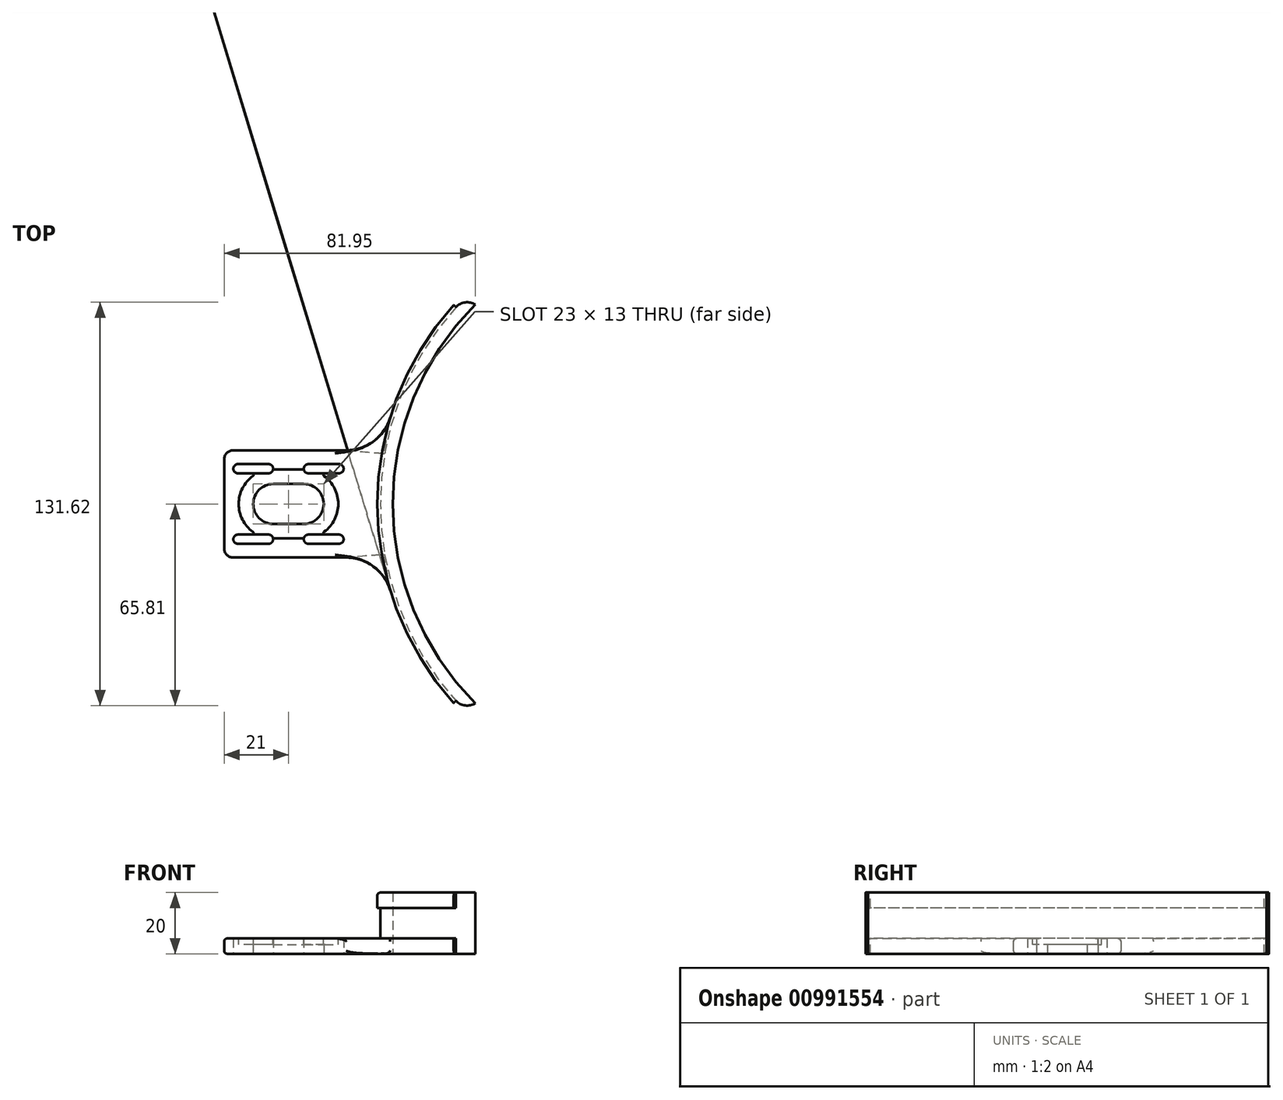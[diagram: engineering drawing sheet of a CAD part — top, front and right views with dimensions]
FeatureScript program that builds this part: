
annotation { "Feature Type Name" : "Feature", "Feature Type Description" : "" }
export const myFeature = defineFeature(function(context is Context, id is Id, definition is map)
    precondition{}
    {
        {
            var Q0;
            Q0=qCreatedBy(makeId("Top.planeOp"),FACE);
            var sketch = newSketch(context, id + "F0", { "sketchPlane" : qUnion([Q0])});
            skPoint(sketch, "E0", {"position": v(92, 0) * mm});
            skLineSegment(sketch, "E1", {"start": v(92, 0) * mm, "end": v(-64.87, 0) * mm, "construction": true});
            skLineSegment(sketch, "E2", {"start": v(92, 0) * mm, "end": v(-16.43, 108.43) * mm, "construction": true});
            skLineSegment(sketch, "E3", {"start": v(92, 0) * mm, "end": v(-13.59, -105.59) * mm, "construction": true});
            skArc(sketch, "E4", {"start": v(26.95, 65.05) * mm, "mid": v(0, 0) * mm, "end": v(26.95, -65.05) * mm});
            skArc(sketch, "E5", {"start": v(24.12, 67.88) * mm, "mid": v(-4, 0) * mm, "end": v(24.12, -67.88) * mm});
            skLineSegment(sketch, "E6", {"start": v(26.95, 65.05) * mm, "end": v(24.12, 67.88) * mm});
            skLineSegment(sketch, "E7", {"start": v(26.95, -65.05) * mm, "end": v(24.12, -67.88) * mm});
            skSolve(sketch);
        }
        {
            var Q0;
            Q0 = qSketchRegion(id + "F0", true);
            extrude(context, id + "F1", {"entities" : qUnion([Q0]), "depth" : 20 * mm, "offsetDistance" : 25 * mm});
        }
        {
            var Q0;
            Q0=qCreatedBy(makeId("Top.planeOp"),FACE);
            var sketch = newSketch(context, id + "F2", { "sketchPlane" : qUnion([Q0])});
            skLineSegment(sketch, "E8.bottom", {"start": v(0, 17.5) * mm, "end": v(-55, 17.5) * mm});
            skLineSegment(sketch, "E8.top", {"start": v(0, -17.5) * mm, "end": v(-55, -17.5) * mm});
            skLineSegment(sketch, "E8.left", {"start": v(0, 17.5) * mm, "end": v(0, -17.5) * mm});
            skLineSegment(sketch, "E8.right", {"start": v(-55, 17.5) * mm, "end": v(-55, -17.5) * mm});
            skPoint(sketch, "E8.middle", {"position": v(-27.5, 0) * mm});
            skSolve(sketch);
        }
        {
            var Q0;
            Q0 = qSketchRegion(id + "F2", true);
            extrude(context, id + "F3", {"entities" : qUnion([Q0]), "operationType" : NewBodyOperationType.ADD, "depth" : 5 * mm, "offsetDistance" : 25 * mm});
        }
        {
            var Q0;
            Q0=makeQuery(id+"F1.opExtrude","CAP_FACE",FACE,{"disambiguationData":[OSD([sQuery(id+"F0.wireOp",EDGE,"E4"),sQuery(id+"F0.wireOp",EDGE,"E5"),sQuery(id+"F0.wireOp",EDGE,"E6"),sQuery(id+"F0.wireOp",EDGE,"E7")])],"isStart":false});
            var sketch = newSketch(context, id + "F4", { "sketchPlane" : qUnion([Q0])});
            skPoint(sketch, "E9", {"position": v(92, 0) * mm});
            skLineSegment(sketch, "E10", {"start": v(92, 0) * mm, "end": v(-2.81, -85.37) * mm, "construction": true});
            skLineSegment(sketch, "E11", {"start": v(92, 0) * mm, "end": v(-2.76, 85.32) * mm, "construction": true});
            skArc(sketch, "E12", {"start": v(20.66, 64.24) * mm, "mid": v(-4, 0) * mm, "end": v(20.66, -64.24) * mm});
            skArc(sketch, "E13", {"start": v(19.91, 64.9) * mm, "mid": v(-5, 0) * mm, "end": v(19.91, -64.9) * mm});
            skLineSegment(sketch, "E14", {"start": v(19.91, 64.9) * mm, "end": v(20.66, 64.24) * mm});
            skLineSegment(sketch, "E15", {"start": v(19.91, -64.9) * mm, "end": v(20.66, -64.24) * mm});
            skSolve(sketch);
        }
        {
            var Q0;
            Q0 = qSketchRegion(id + "F4", true);
            extrude(context, id + "F5", {"entities" : qUnion([Q0]), "operationType" : NewBodyOperationType.ADD, "oppositeDirection" : true, "depth" : 5 * mm, "offsetDistance" : 25 * mm});
        }
        {
            var Q0;
            Q0=makeQuery(id+"F3.boolean.opBoolean","MERGE",FACE,{"derivedFrom":[makeQuery(id+"F1.opExtrude","CAP_FACE",FACE,{"disambiguationData":[OSD([sQuery(id+"F0.wireOp",EDGE,"E4"),sQuery(id+"F0.wireOp",EDGE,"E5"),sQuery(id+"F0.wireOp",EDGE,"E6"),sQuery(id+"F0.wireOp",EDGE,"E7")])],"isStart":true}),makeQuery(id+"F3.opExtrude","CAP_FACE",FACE,{"disambiguationData":[OSD([sQuery(id+"F2.wireOp",EDGE,"E8.bottom"),sQuery(id+"F2.wireOp",EDGE,"E8.top"),sQuery(id+"F2.wireOp",EDGE,"E8.left"),sQuery(id+"F2.wireOp",EDGE,"E8.right")])],"isStart":true})]});
            var Q1;
            Q1=makeQuery(id+"F3.boolean.opBoolean","MERGE",FACE,{"derivedFrom":[makeQuery(id+"F1.opExtrude","CAP_FACE",FACE,{"disambiguationData":[OSD([sQuery(id+"F0.wireOp",EDGE,"E4"),sQuery(id+"F0.wireOp",EDGE,"E5"),sQuery(id+"F0.wireOp",EDGE,"E6"),sQuery(id+"F0.wireOp",EDGE,"E7")])],"isStart":true}),makeQuery(id+"F3.opExtrude","CAP_FACE",FACE,{"disambiguationData":[OSD([sQuery(id+"F2.wireOp",EDGE,"E8.bottom"),sQuery(id+"F2.wireOp",EDGE,"E8.top"),sQuery(id+"F2.wireOp",EDGE,"E8.left"),sQuery(id+"F2.wireOp",EDGE,"E8.right")])],"isStart":true})]});
            var sketch = newSketch(context, id + "F6", { "sketchPlane" : qUnion([Q0, Q1])});
            skPoint(sketch, "E16", {"position": v(92, 0) * mm});
            skLineSegment(sketch, "E17", {"start": v(92, 0) * mm, "end": v(6.61, -76.88) * mm, "construction": true});
            skLineSegment(sketch, "E18", {"start": v(92, 0) * mm, "end": v(0.37, 82.5) * mm, "construction": true});
            skLineSegment(sketch, "E19", {"start": v(92, 0) * mm, "end": v(0, 0) * mm, "construction": true});
            skArc(sketch, "E20", {"start": v(20.66, 64.24) * mm, "mid": v(-4, 0) * mm, "end": v(20.66, -64.24) * mm});
            skArc(sketch, "E21", {"start": v(19.91, 64.9) * mm, "mid": v(-5, 0) * mm, "end": v(19.91, -64.9) * mm});
            skLineSegment(sketch, "E22", {"start": v(19.91, 64.9) * mm, "end": v(20.66, 64.24) * mm});
            skLineSegment(sketch, "E23", {"start": v(19.91, -64.9) * mm, "end": v(20.66, -64.24) * mm});
            skSolve(sketch);
        }
        {
            var Q0;
            Q0 = qSketchRegion(id + "F6", true);
            extrude(context, id + "F7", {"entities" : qUnion([Q0]), "operationType" : NewBodyOperationType.ADD, "oppositeDirection" : true, "depth" : 5 * mm, "offsetDistance" : 25 * mm});
        }
        {
            var Q0;
            Q0=makeQuery(id+"F7.boolean.opBoolean","MERGE",FACE,{"derivedFrom":[makeQuery(id+"F3.boolean.opBoolean","MERGE",FACE,{"derivedFrom":[makeQuery(id+"F1.opExtrude","CAP_FACE",FACE,{"disambiguationData":[OSD([sQuery(id+"F0.wireOp",EDGE,"E4"),sQuery(id+"F0.wireOp",EDGE,"E5"),sQuery(id+"F0.wireOp",EDGE,"E6"),sQuery(id+"F0.wireOp",EDGE,"E7")])],"isStart":true}),makeQuery(id+"F3.opExtrude","CAP_FACE",FACE,{"disambiguationData":[OSD([sQuery(id+"F2.wireOp",EDGE,"E8.bottom"),sQuery(id+"F2.wireOp",EDGE,"E8.top"),sQuery(id+"F2.wireOp",EDGE,"E8.left"),sQuery(id+"F2.wireOp",EDGE,"E8.right")])],"isStart":true})]}),makeQuery(id+"F7.opExtrude","CAP_FACE",FACE,{"disambiguationData":[OSD([sQuery(id+"F6.wireOp",EDGE,"E20"),sQuery(id+"F6.wireOp",EDGE,"E21"),sQuery(id+"F6.wireOp",EDGE,"E22"),sQuery(id+"F6.wireOp",EDGE,"E23")])],"isStart":true})]});
            var sketch = newSketch(context, id + "F8", { "sketchPlane" : qUnion([Q0])});
            skPoint(sketch, "E24", {"position": v(-34, 0) * mm});
            skLineSegment(sketch, "E25", {"start": v(-39, 0) * mm, "end": v(-29, 0) * mm, "construction": true});
            skArc(sketch, "E26.0.startCap", {"start": v(-39, -6.5) * mm, "mid": v(-45.5, 0) * mm, "end": v(-39, 6.5) * mm});
            skArc(sketch, "E26.0.endCap", {"start": v(-29, 6.5) * mm, "mid": v(-22.5, 0) * mm, "end": v(-29, -6.5) * mm});
            skLineSegment(sketch, "E26.0.left", {"start": v(-39, 6.5) * mm, "end": v(-29, 6.5) * mm});
            skLineSegment(sketch, "E26.0.right", {"start": v(-39, -6.5) * mm, "end": v(-29, -6.5) * mm});
            skLineSegment(sketch, "E27", {"start": v(-34, 14.73) * mm, "end": v(-34, -13.9) * mm, "construction": true});
            skLineSegment(sketch, "E28", {"start": v(-53.74, 0) * mm, "end": v(-13.22, 0) * mm, "construction": true});
            skLineSegment(sketch, "E29", {"start": v(-29, 25.63) * mm, "end": v(-29, -27.09) * mm, "construction": true});
            skLineSegment(sketch, "E30", {"start": v(-39, -27.74) * mm, "end": v(-39, 26.77) * mm, "construction": true});
            skLineSegment(sketch, "E31", {"start": v(-17.5, 11.5) * mm, "end": v(-27.5, 11.5) * mm, "construction": true});
            skLineSegment(sketch, "E32", {"start": v(-17.5, -11.5) * mm, "end": v(-27.5, -11.5) * mm, "construction": true});
            skLineSegment(sketch, "E33", {"start": v(-40.5, -11.5) * mm, "end": v(-50.5, -11.5) * mm, "construction": true});
            skLineSegment(sketch, "E34", {"start": v(-40.5, 11.5) * mm, "end": v(-50.5, 11.5) * mm, "construction": true});
            skArc(sketch, "E35.0.startCap", {"start": v(-17.5, 13) * mm, "mid": v(-16, 11.5) * mm, "end": v(-17.5, 10) * mm});
            skArc(sketch, "E35.0.endCap", {"start": v(-27.5, 10) * mm, "mid": v(-29, 11.5) * mm, "end": v(-27.5, 13) * mm});
            skLineSegment(sketch, "E35.0.left", {"start": v(-17.5, 10) * mm, "end": v(-27.5, 10) * mm});
            skLineSegment(sketch, "E35.0.right", {"start": v(-17.5, 13) * mm, "end": v(-27.5, 13) * mm});
            skArc(sketch, "E36.0.startCap", {"start": v(-40.5, 13) * mm, "mid": v(-39, 11.5) * mm, "end": v(-40.5, 10) * mm});
            skArc(sketch, "E36.0.endCap", {"start": v(-50.5, 10) * mm, "mid": v(-52, 11.5) * mm, "end": v(-50.5, 13) * mm});
            skLineSegment(sketch, "E36.0.left", {"start": v(-40.5, 10) * mm, "end": v(-50.5, 10) * mm});
            skLineSegment(sketch, "E36.0.right", {"start": v(-40.5, 13) * mm, "end": v(-50.5, 13) * mm});
            skArc(sketch, "E37.0.startCap", {"start": v(-40.5, -10) * mm, "mid": v(-39, -11.5) * mm, "end": v(-40.5, -13) * mm});
            skArc(sketch, "E37.0.endCap", {"start": v(-50.5, -13) * mm, "mid": v(-52, -11.5) * mm, "end": v(-50.5, -10) * mm});
            skLineSegment(sketch, "E37.0.left", {"start": v(-40.5, -13) * mm, "end": v(-50.5, -13) * mm});
            skLineSegment(sketch, "E37.0.right", {"start": v(-40.5, -10) * mm, "end": v(-50.5, -10) * mm});
            skArc(sketch, "E37.1.startCap", {"start": v(-17.5, -10) * mm, "mid": v(-16, -11.5) * mm, "end": v(-17.5, -13) * mm});
            skArc(sketch, "E37.1.endCap", {"start": v(-27.5, -13) * mm, "mid": v(-29, -11.5) * mm, "end": v(-27.5, -10) * mm});
            skLineSegment(sketch, "E37.1.left", {"start": v(-17.5, -13) * mm, "end": v(-27.5, -13) * mm});
            skLineSegment(sketch, "E37.1.right", {"start": v(-17.5, -10) * mm, "end": v(-27.5, -10) * mm});
            skSolve(sketch);
        }
        {
            var Q0;
            Q0 = qSketchRegion(id + "F8", true);
            extrude(context, id + "F9", {"entities" : qUnion([Q0]), "operationType" : NewBodyOperationType.REMOVE, "oppositeDirection" : true, "depth" : 8 * mm, "offsetDistance" : 25 * mm});
        }
        {
            var Q0;
            Q0=makeQuery(id+"F7.boolean.opBoolean","MERGE",FACE,{"derivedFrom":[makeQuery(id+"F3.opExtrude","CAP_FACE",FACE,{"disambiguationData":[OSD([sQuery(id+"F2.wireOp",EDGE,"E8.bottom"),sQuery(id+"F2.wireOp",EDGE,"E8.top"),sQuery(id+"F2.wireOp",EDGE,"E8.left"),sQuery(id+"F2.wireOp",EDGE,"E8.right")])],"isStart":false}),makeQuery(id+"F7.opExtrude","CAP_FACE",FACE,{"disambiguationData":[OSD([sQuery(id+"F6.wireOp",EDGE,"E20"),sQuery(id+"F6.wireOp",EDGE,"E21"),sQuery(id+"F6.wireOp",EDGE,"E22"),sQuery(id+"F6.wireOp",EDGE,"E23")])],"isStart":false})]});
            var sketch = newSketch(context, id + "F10", { "sketchPlane" : qUnion([Q0])});
            skLineSegment(sketch, "E38", {"start": v(-39, 0) * mm, "end": v(-29, 0) * mm, "construction": true});
            skArc(sketch, "E39.0.startCap", {"start": v(-39, -11.25) * mm, "mid": v(-50.25, 0) * mm, "end": v(-39, 11.25) * mm});
            skArc(sketch, "E39.0.endCap", {"start": v(-29, 11.25) * mm, "mid": v(-17.75, 0) * mm, "end": v(-29, -11.25) * mm});
            skLineSegment(sketch, "E39.0.left", {"start": v(-39, 11.25) * mm, "end": v(-29, 11.25) * mm});
            skLineSegment(sketch, "E39.0.right", {"start": v(-39, -11.25) * mm, "end": v(-29, -11.25) * mm});
            skSolve(sketch);
        }
        {
            var Q0;
            Q0 = qSketchRegion(id + "F10", true);
            extrude(context, id + "F11", {"entities" : qUnion([Q0]), "operationType" : NewBodyOperationType.REMOVE, "oppositeDirection" : true, "depth" : 2.05 * mm, "offsetDistance" : 25 * mm});
        }
        {
            var Q0;
            Q0=makeQuery(id+"F1.opExtrude","SWEPT_EDGE",EDGE,{"disambiguationData":[OSD([sQuery(id+"F0.wireOp",EDGE,"E5"),sQuery(id+"F0.wireOp",EDGE,"E7")])]});
            var Q1;
            Q1=makeQuery(id+"F1.opExtrude","SWEPT_EDGE",EDGE,{"disambiguationData":[OSD([sQuery(id+"F0.wireOp",EDGE,"E5"),sQuery(id+"F0.wireOp",EDGE,"E6")])]});
            fillet(context, id + "F12", {"entities" : qUnion([Q0, Q1]), "radius" : 5 * mm, "tangentPropagation" : true, "allowEdgeOverflow" : false});
        }
        {
            var Q0;
            Q0=makeQuery(id+"F3.opExtrude","SWEPT_EDGE",EDGE,{"disambiguationData":[OSD([sQuery(id+"F2.wireOp",EDGE,"E8.top"),sQuery(id+"F2.wireOp",EDGE,"E8.right")])]});
            var Q1;
            Q1=makeQuery(id+"F3.opExtrude","SWEPT_EDGE",EDGE,{"disambiguationData":[OSD([sQuery(id+"F2.wireOp",EDGE,"E8.bottom"),sQuery(id+"F2.wireOp",EDGE,"E8.right")])]});
            fillet(context, id + "F13", {"entities" : qUnion([Q0, Q1]), "radius" : 3 * mm, "tangentPropagation" : true, "allowEdgeOverflow" : false});
        }
        {
            var Q0;
            Q0=makeQuery(id+"F5.opExtrude","CAP_EDGE",EDGE,{"disambiguationData":[OSD([sQuery(id+"F4.wireOp",EDGE,"E13")])],"isStart":true});
            var Q1;
            {var subQ1=sQuery(id+"F6.wireOp",EDGE,"E21");var subQ2=sQuery(id+"F2.wireOp",EDGE,"E8.top");Q1=makeQuery(id+"F7.boolean.opBoolean","SPLIT",EDGE,{"disambiguationData":[TD([makeQuery(id+"F3.opExtrude","SWEPT_FACE",FACE,{"disambiguationData":[OSD([subQ2])]})])],"derivedFrom":makeQuery(id+"F7.opExtrude","CAP_EDGE",EDGE,{"disambiguationData":[OSD([subQ1])],"isStart":true})});}
            var Q2;
            {var subQ1=sQuery(id+"F6.wireOp",EDGE,"E21");var subQ2=sQuery(id+"F2.wireOp",EDGE,"E8.bottom");Q2=makeQuery(id+"F7.boolean.opBoolean","SPLIT",EDGE,{"disambiguationData":[TD([makeQuery(id+"F3.opExtrude","SWEPT_FACE",FACE,{"disambiguationData":[OSD([subQ2])]})])],"derivedFrom":makeQuery(id+"F7.opExtrude","CAP_EDGE",EDGE,{"disambiguationData":[OSD([subQ1])],"isStart":true})});}
            fillet(context, id + "F14", {"entities" : qUnion([Q0, Q1, Q2]), "radius" : 1 * mm, "tangentPropagation" : true, "allowEdgeOverflow" : false});
        }
        {
            var Q0;
            Q0=makeQuery(id+"F3.opExtrude","CAP_EDGE",EDGE,{"disambiguationData":[OSD([sQuery(id+"F2.wireOp",EDGE,"E8.top")])],"isStart":true});
            var Q1;
            {var subQ0=sQuery(id+"F2.wireOp",EDGE,"E8.right");var subQ1=sQuery(id+"F2.wireOp",EDGE,"E8.top");Q1=makeQuery(id+"F13.opFillet","BLEND_EDGE",EDGE,{"blendedFrom":[makeQuery(id+"F3.opExtrude","SWEPT_EDGE",EDGE,{"disambiguationData":[OSD([subQ1,subQ0])]}),makeQuery(id+"F7.boolean.opBoolean","MERGE",FACE,{"derivedFrom":[makeQuery(id+"F3.boolean.opBoolean","MERGE",FACE,{"derivedFrom":[makeQuery(id+"F1.opExtrude","CAP_FACE",FACE,{"disambiguationData":[OSD([sQuery(id+"F0.wireOp",EDGE,"E4"),sQuery(id+"F0.wireOp",EDGE,"E5"),sQuery(id+"F0.wireOp",EDGE,"E6"),sQuery(id+"F0.wireOp",EDGE,"E7")])],"isStart":true}),makeQuery(id+"F3.opExtrude","CAP_FACE",FACE,{"disambiguationData":[OSD([sQuery(id+"F2.wireOp",EDGE,"E8.bottom"),subQ1,sQuery(id+"F2.wireOp",EDGE,"E8.left"),subQ0])],"isStart":true})]}),makeQuery(id+"F7.opExtrude","CAP_FACE",FACE,{"disambiguationData":[OSD([sQuery(id+"F6.wireOp",EDGE,"E20"),sQuery(id+"F6.wireOp",EDGE,"E21"),sQuery(id+"F6.wireOp",EDGE,"E22"),sQuery(id+"F6.wireOp",EDGE,"E23")])],"isStart":true})]})],"blendedInto":[makeQuery(id+"F7.boolean.opBoolean","MERGE",FACE,{"derivedFrom":[makeQuery(id+"F3.boolean.opBoolean","MERGE",FACE,{"derivedFrom":[makeQuery(id+"F1.opExtrude","CAP_FACE",FACE,{"disambiguationData":[OSD([sQuery(id+"F0.wireOp",EDGE,"E4"),sQuery(id+"F0.wireOp",EDGE,"E5"),sQuery(id+"F0.wireOp",EDGE,"E6"),sQuery(id+"F0.wireOp",EDGE,"E7")])],"isStart":true}),makeQuery(id+"F3.opExtrude","CAP_FACE",FACE,{"disambiguationData":[OSD([sQuery(id+"F2.wireOp",EDGE,"E8.bottom"),subQ1,sQuery(id+"F2.wireOp",EDGE,"E8.left"),subQ0])],"isStart":true})]}),makeQuery(id+"F7.opExtrude","CAP_FACE",FACE,{"disambiguationData":[OSD([sQuery(id+"F6.wireOp",EDGE,"E20"),sQuery(id+"F6.wireOp",EDGE,"E21"),sQuery(id+"F6.wireOp",EDGE,"E22"),sQuery(id+"F6.wireOp",EDGE,"E23")])],"isStart":true})]})]});}
            var Q2;
            Q2=makeQuery(id+"F3.opExtrude","CAP_EDGE",EDGE,{"disambiguationData":[OSD([sQuery(id+"F2.wireOp",EDGE,"E8.right")])],"isStart":true});
            var Q3;
            {var subQ0=sQuery(id+"F2.wireOp",EDGE,"E8.right");var subQ1=sQuery(id+"F2.wireOp",EDGE,"E8.bottom");Q3=makeQuery(id+"F13.opFillet","BLEND_EDGE",EDGE,{"blendedFrom":[makeQuery(id+"F3.opExtrude","SWEPT_EDGE",EDGE,{"disambiguationData":[OSD([subQ1,subQ0])]}),makeQuery(id+"F7.boolean.opBoolean","MERGE",FACE,{"derivedFrom":[makeQuery(id+"F3.boolean.opBoolean","MERGE",FACE,{"derivedFrom":[makeQuery(id+"F1.opExtrude","CAP_FACE",FACE,{"disambiguationData":[OSD([sQuery(id+"F0.wireOp",EDGE,"E4"),sQuery(id+"F0.wireOp",EDGE,"E5"),sQuery(id+"F0.wireOp",EDGE,"E6"),sQuery(id+"F0.wireOp",EDGE,"E7")])],"isStart":true}),makeQuery(id+"F3.opExtrude","CAP_FACE",FACE,{"disambiguationData":[OSD([subQ1,sQuery(id+"F2.wireOp",EDGE,"E8.top"),sQuery(id+"F2.wireOp",EDGE,"E8.left"),subQ0])],"isStart":true})]}),makeQuery(id+"F7.opExtrude","CAP_FACE",FACE,{"disambiguationData":[OSD([sQuery(id+"F6.wireOp",EDGE,"E20"),sQuery(id+"F6.wireOp",EDGE,"E21"),sQuery(id+"F6.wireOp",EDGE,"E22"),sQuery(id+"F6.wireOp",EDGE,"E23")])],"isStart":true})]})],"blendedInto":[makeQuery(id+"F7.boolean.opBoolean","MERGE",FACE,{"derivedFrom":[makeQuery(id+"F3.boolean.opBoolean","MERGE",FACE,{"derivedFrom":[makeQuery(id+"F1.opExtrude","CAP_FACE",FACE,{"disambiguationData":[OSD([sQuery(id+"F0.wireOp",EDGE,"E4"),sQuery(id+"F0.wireOp",EDGE,"E5"),sQuery(id+"F0.wireOp",EDGE,"E6"),sQuery(id+"F0.wireOp",EDGE,"E7")])],"isStart":true}),makeQuery(id+"F3.opExtrude","CAP_FACE",FACE,{"disambiguationData":[OSD([subQ1,sQuery(id+"F2.wireOp",EDGE,"E8.top"),sQuery(id+"F2.wireOp",EDGE,"E8.left"),subQ0])],"isStart":true})]}),makeQuery(id+"F7.opExtrude","CAP_FACE",FACE,{"disambiguationData":[OSD([sQuery(id+"F6.wireOp",EDGE,"E20"),sQuery(id+"F6.wireOp",EDGE,"E21"),sQuery(id+"F6.wireOp",EDGE,"E22"),sQuery(id+"F6.wireOp",EDGE,"E23")])],"isStart":true})]})]});}
            var Q4;
            Q4=makeQuery(id+"F3.opExtrude","CAP_EDGE",EDGE,{"disambiguationData":[OSD([sQuery(id+"F2.wireOp",EDGE,"E8.bottom")])],"isStart":true});
            fillet(context, id + "F15", {"entities" : qUnion([Q0, Q1, Q2, Q3, Q4]), "radius" : 1 * mm, "tangentPropagation" : true, "allowEdgeOverflow" : false});
        }
        {
            var Q0;
            Q0=makeQuery(id+"F3.opExtrude","CAP_EDGE",EDGE,{"disambiguationData":[OSD([sQuery(id+"F2.wireOp",EDGE,"E8.bottom")])],"isStart":false});
            var Q1;
            {var subQ0=sQuery(id+"F2.wireOp",EDGE,"E8.right");var subQ1=sQuery(id+"F2.wireOp",EDGE,"E8.bottom");Q1=makeQuery(id+"F13.opFillet","BLEND_EDGE",EDGE,{"blendedFrom":[makeQuery(id+"F3.opExtrude","SWEPT_EDGE",EDGE,{"disambiguationData":[OSD([subQ1,subQ0])]}),makeQuery(id+"F7.boolean.opBoolean","MERGE",FACE,{"derivedFrom":[makeQuery(id+"F3.opExtrude","CAP_FACE",FACE,{"disambiguationData":[OSD([subQ1,sQuery(id+"F2.wireOp",EDGE,"E8.top"),sQuery(id+"F2.wireOp",EDGE,"E8.left"),subQ0])],"isStart":false}),makeQuery(id+"F7.opExtrude","CAP_FACE",FACE,{"disambiguationData":[OSD([sQuery(id+"F6.wireOp",EDGE,"E20"),sQuery(id+"F6.wireOp",EDGE,"E21"),sQuery(id+"F6.wireOp",EDGE,"E22"),sQuery(id+"F6.wireOp",EDGE,"E23")])],"isStart":false})]})],"blendedInto":[makeQuery(id+"F7.boolean.opBoolean","MERGE",FACE,{"derivedFrom":[makeQuery(id+"F3.opExtrude","CAP_FACE",FACE,{"disambiguationData":[OSD([subQ1,sQuery(id+"F2.wireOp",EDGE,"E8.top"),sQuery(id+"F2.wireOp",EDGE,"E8.left"),subQ0])],"isStart":false}),makeQuery(id+"F7.opExtrude","CAP_FACE",FACE,{"disambiguationData":[OSD([sQuery(id+"F6.wireOp",EDGE,"E20"),sQuery(id+"F6.wireOp",EDGE,"E21"),sQuery(id+"F6.wireOp",EDGE,"E22"),sQuery(id+"F6.wireOp",EDGE,"E23")])],"isStart":false})]})]});}
            var Q2;
            Q2=makeQuery(id+"F3.opExtrude","CAP_EDGE",EDGE,{"disambiguationData":[OSD([sQuery(id+"F2.wireOp",EDGE,"E8.right")])],"isStart":false});
            var Q3;
            {var subQ0=sQuery(id+"F2.wireOp",EDGE,"E8.right");var subQ1=sQuery(id+"F2.wireOp",EDGE,"E8.top");Q3=makeQuery(id+"F13.opFillet","BLEND_EDGE",EDGE,{"blendedFrom":[makeQuery(id+"F3.opExtrude","SWEPT_EDGE",EDGE,{"disambiguationData":[OSD([subQ1,subQ0])]}),makeQuery(id+"F7.boolean.opBoolean","MERGE",FACE,{"derivedFrom":[makeQuery(id+"F3.opExtrude","CAP_FACE",FACE,{"disambiguationData":[OSD([sQuery(id+"F2.wireOp",EDGE,"E8.bottom"),subQ1,sQuery(id+"F2.wireOp",EDGE,"E8.left"),subQ0])],"isStart":false}),makeQuery(id+"F7.opExtrude","CAP_FACE",FACE,{"disambiguationData":[OSD([sQuery(id+"F6.wireOp",EDGE,"E20"),sQuery(id+"F6.wireOp",EDGE,"E21"),sQuery(id+"F6.wireOp",EDGE,"E22"),sQuery(id+"F6.wireOp",EDGE,"E23")])],"isStart":false})]})],"blendedInto":[makeQuery(id+"F7.boolean.opBoolean","MERGE",FACE,{"derivedFrom":[makeQuery(id+"F3.opExtrude","CAP_FACE",FACE,{"disambiguationData":[OSD([sQuery(id+"F2.wireOp",EDGE,"E8.bottom"),subQ1,sQuery(id+"F2.wireOp",EDGE,"E8.left"),subQ0])],"isStart":false}),makeQuery(id+"F7.opExtrude","CAP_FACE",FACE,{"disambiguationData":[OSD([sQuery(id+"F6.wireOp",EDGE,"E20"),sQuery(id+"F6.wireOp",EDGE,"E21"),sQuery(id+"F6.wireOp",EDGE,"E22"),sQuery(id+"F6.wireOp",EDGE,"E23")])],"isStart":false})]})]});}
            var Q4;
            Q4=makeQuery(id+"F3.opExtrude","CAP_EDGE",EDGE,{"disambiguationData":[OSD([sQuery(id+"F2.wireOp",EDGE,"E8.top")])],"isStart":false});
            fillet(context, id + "F16", {"entities" : qUnion([Q0, Q1, Q2, Q3, Q4]), "radius" : 1 * mm, "tangentPropagation" : true, "allowEdgeOverflow" : false});
        }
        {
            var Q0;
            Q0=makeQuery(id+"F11.boolean.opBoolean","INTERSECT",EDGE,{"derivedFrom":[makeQuery(id+"F9.boolean.opBoolean","COPY",FACE,{"derivedFrom":makeQuery(id+"F9.opExtrude","SWEPT_FACE",FACE,{"disambiguationData":[OSD([sQuery(id+"F8.wireOp",EDGE,"E37.0.right")])]})}),makeQuery(id+"F11.opExtrude","SWEPT_FACE",FACE,{"disambiguationData":[OSD([sQuery(id+"F10.wireOp",EDGE,"E39.0.startCap")])]})]});
            var Q1;
            Q1=makeQuery(id+"F11.boolean.opBoolean","INTERSECT",EDGE,{"derivedFrom":[makeQuery(id+"F9.boolean.opBoolean","COPY",FACE,{"derivedFrom":makeQuery(id+"F9.opExtrude","SWEPT_FACE",FACE,{"disambiguationData":[OSD([sQuery(id+"F8.wireOp",EDGE,"E37.1.right")])]})}),makeQuery(id+"F11.opExtrude","SWEPT_FACE",FACE,{"disambiguationData":[OSD([sQuery(id+"F10.wireOp",EDGE,"E39.0.endCap")])]})]});
            var Q2;
            Q2=makeQuery(id+"F11.boolean.opBoolean","INTERSECT",EDGE,{"derivedFrom":[makeQuery(id+"F9.boolean.opBoolean","COPY",FACE,{"derivedFrom":makeQuery(id+"F9.opExtrude","SWEPT_FACE",FACE,{"disambiguationData":[OSD([sQuery(id+"F8.wireOp",EDGE,"E35.0.left")])]})}),makeQuery(id+"F11.opExtrude","SWEPT_FACE",FACE,{"disambiguationData":[OSD([sQuery(id+"F10.wireOp",EDGE,"E39.0.endCap")])]})]});
            var Q3;
            Q3=makeQuery(id+"F11.boolean.opBoolean","INTERSECT",EDGE,{"derivedFrom":[makeQuery(id+"F9.boolean.opBoolean","COPY",FACE,{"derivedFrom":makeQuery(id+"F9.opExtrude","SWEPT_FACE",FACE,{"disambiguationData":[OSD([sQuery(id+"F8.wireOp",EDGE,"E36.0.left")])]})}),makeQuery(id+"F11.opExtrude","SWEPT_FACE",FACE,{"disambiguationData":[OSD([sQuery(id+"F10.wireOp",EDGE,"E39.0.startCap")])]})]});
            fillet(context, id + "F17", {"entities" : qUnion([Q0, Q1, Q2, Q3]), "radius" : 0.5 * mm, "tangentPropagation" : true, "allowEdgeOverflow" : false});
        }
        {
            var Q0;
            Q0=makeQuery(id+"F7.boolean.opBoolean","INTERSECT",EDGE,{"derivedFrom":[makeQuery(id+"F3.opExtrude","SWEPT_FACE",FACE,{"disambiguationData":[OSD([sQuery(id+"F2.wireOp",EDGE,"E8.top")])]}),makeQuery(id+"F7.opExtrude","SWEPT_FACE",FACE,{"disambiguationData":[OSD([sQuery(id+"F6.wireOp",EDGE,"E21")])]})]});
            var Q1;
            Q1=makeQuery(id+"F7.boolean.opBoolean","INTERSECT",EDGE,{"derivedFrom":[makeQuery(id+"F3.opExtrude","SWEPT_FACE",FACE,{"disambiguationData":[OSD([sQuery(id+"F2.wireOp",EDGE,"E8.bottom")])]}),makeQuery(id+"F7.opExtrude","SWEPT_FACE",FACE,{"disambiguationData":[OSD([sQuery(id+"F6.wireOp",EDGE,"E21")])]})]});
            fillet(context, id + "F18", {"entities" : qUnion([Q0, Q1]), "radius" : 15 * mm, "tangentPropagation" : true, "allowEdgeOverflow" : false});
        }
    });
